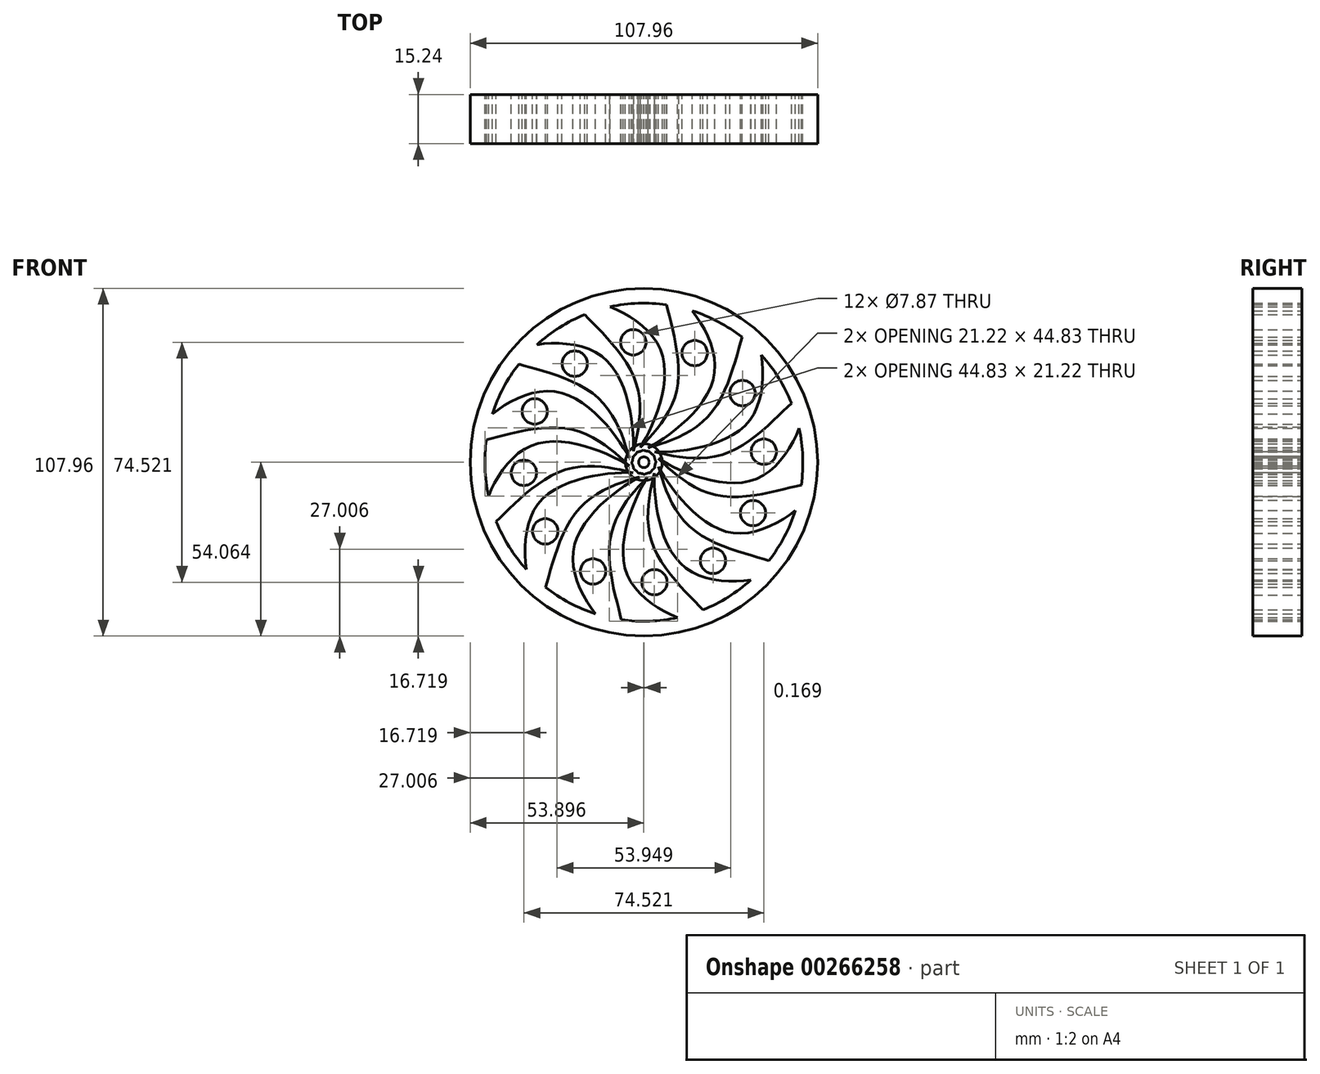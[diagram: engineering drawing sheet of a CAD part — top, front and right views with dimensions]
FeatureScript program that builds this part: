
annotation { "Feature Type Name" : "Feature", "Feature Type Description" : "" }
export const myFeature = defineFeature(function(context is Context, id is Id, definition is map)
    precondition{}
    {
        {
            var Q0;
            Q0=qCreatedBy(makeId("Front.planeOp"),FACE);
            var sketch = newSketch(context, id + "F0", { "sketchPlane" : qUnion([Q0])});
            skFitSpline(sketch, "E0", {"points": [v(0, 3.74) * mm, v(19.9, 14.16) * mm, v(32.83, 42.5) * mm, v(32.62, 12.7) * mm, v(0, 3.74) * mm]});
            skCircle(sketch, "E1", {"center": v(30.63, 21.47) * mm, "radius": 3.94 * mm});
            skSolve(sketch);
        }
        {
            var Q0;
            Q0=qCreatedBy(makeId("Right.planeOp"),FACE);
            var sketch = newSketch(context, id + "F1", { "sketchPlane" : qUnion([Q0])});
            skLineSegment(sketch, "E2", {"start": v(0, 0) * mm, "end": v(-29.45, 0) * mm, "construction": true});
            skSolve(sketch);
        }
        {
            var Q0;
            Q0=makeQuery(id+"F0.imprint","IMPRINT",FACE,{"disambiguationData":[TD([[makeQuery(id+"F0.imprint","IMPRINT",EDGE,{"derivedFrom":sQuery(id+"F0.wireOp",EDGE,"E0")}),-1.0]])]});
            extrude(context, id + "F2", {"entities" : qUnion([Q0]), "depth" : 15.24 * mm});
        }
        {
            var Q0;
            Q0=makeQuery(id+"F2.opExtrude","SWEPT_BODY",BODY,{"disambiguationData":[OSD([sQuery(id+"F0.wireOp",EDGE,"E0")])]});
            var Q1;
            Q1=sQuery(id+"F1.wireOp",EDGE,"E2");
            circularPattern(context, id + "F3", {"operationType" : NewBodyOperationType.ADD, "entities" : qUnion([Q0]), "axis" : qUnion([Q1]), "angle" : 360 * degree, "instanceCount" : 12, "equalSpace" : true});
        }
        {
            var Q0;
            Q0=qCreatedBy(makeId("Front.planeOp"),FACE);
            var sketch = newSketch(context, id + "F4", { "sketchPlane" : qUnion([Q0])});
            skCircle(sketch, "E3", {"center": v(0, 0) * mm, "radius": 1.65 * mm});
            skCircle(sketch, "E4", {"center": v(0, 0) * mm, "radius": 5.72 * mm});
            skSolve(sketch);
        }
        {
            var Q0;
            Q0 = qSketchRegion(id + "F4", true);
            extrude(context, id + "F5", {"entities" : qUnion([Q0]), "depth" : 15.24 * mm});
        }
        {
            var Q0;
            Q0=qCreatedBy(makeId("Front.planeOp"),FACE);
            var sketch = newSketch(context, id + "F6", { "sketchPlane" : qUnion([Q0])});
            skCircle(sketch, "E5", {"center": v(0, 0) * mm, "radius": 49.4 * mm});
            skCircle(sketch, "E6", {"center": v(0, 0) * mm, "radius": 53.98 * mm});
            skSolve(sketch);
        }
        {
            var Q0;
            Q0 = qSketchRegion(id + "F6", true);
            extrude(context, id + "F7", {"entities" : qUnion([Q0]), "operationType" : NewBodyOperationType.ADD, "depth" : 15.24 * mm});
        }
    });
